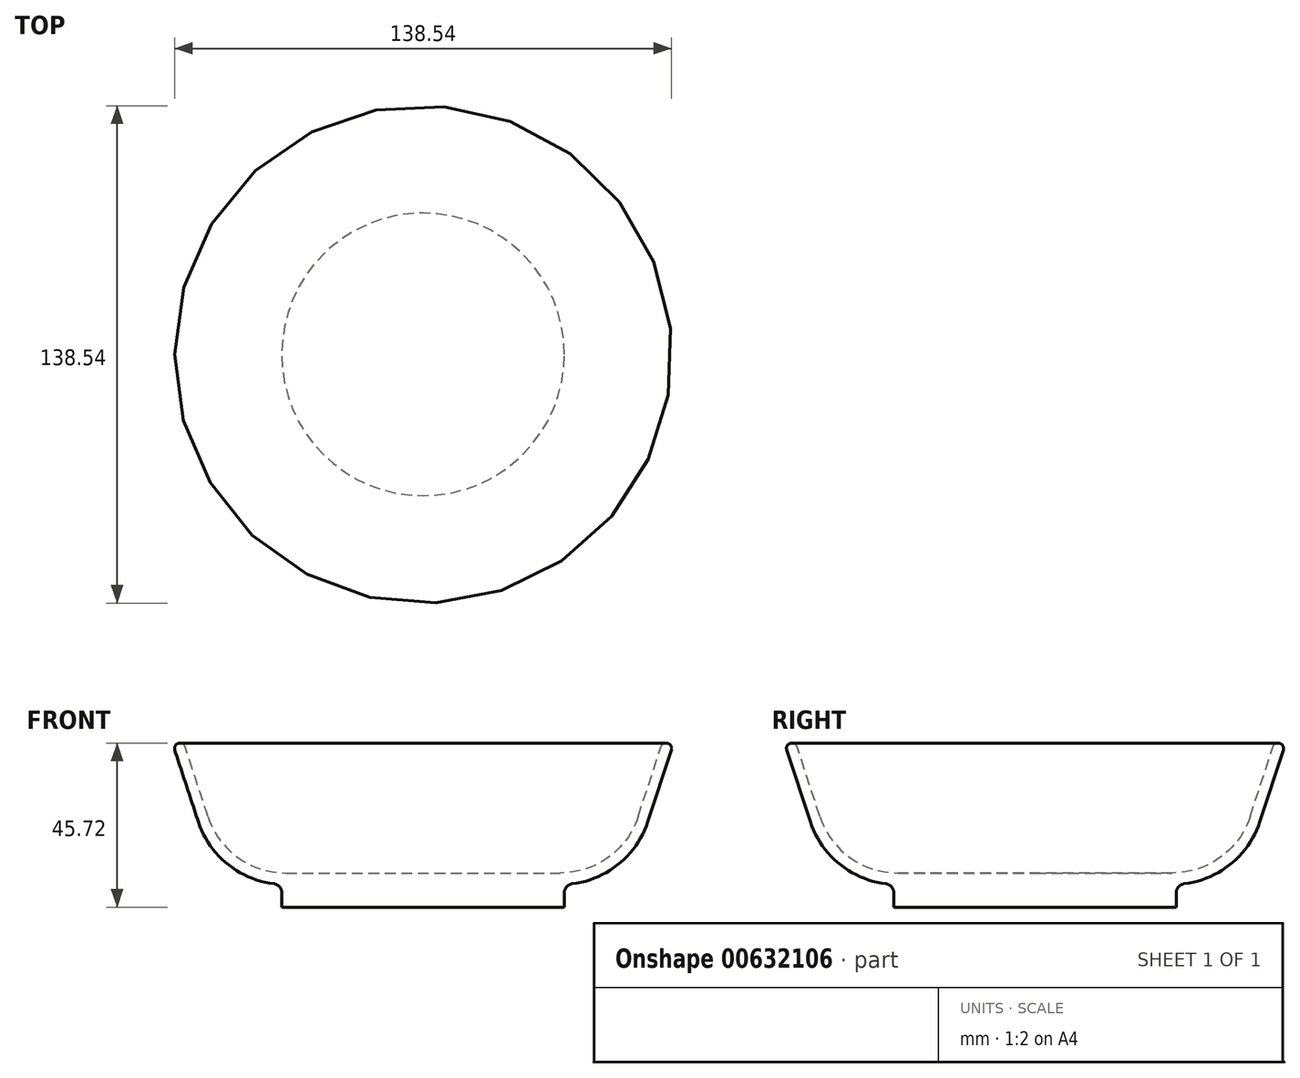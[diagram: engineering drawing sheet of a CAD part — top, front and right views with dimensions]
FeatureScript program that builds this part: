
annotation { "Feature Type Name" : "Feature", "Feature Type Description" : "" }
export const myFeature = defineFeature(function(context is Context, id is Id, definition is map)
    precondition{}
    {
        {
            var Q0;
            Q0=qCreatedBy(makeId("Front.planeOp"),FACE);
            var sketch = newSketch(context, id + "F0", { "sketchPlane" : qUnion([Q0])});
            skLineSegment(sketch, "E0.bottom", {"start": v(-76.2, 0) * mm, "end": v(63.5, 0) * mm, "construction": true});
            skLineSegment(sketch, "E0.top", {"start": v(62.55, 45.72) * mm, "end": v(63.5, 45.72) * mm, "construction": true});
            skLineSegment(sketch, "E0.left", {"start": v(-76.2, 0) * mm, "end": v(-76.2, 45.72) * mm, "construction": true});
            skLineSegment(sketch, "E0.right", {"start": v(63.5, 0) * mm, "end": v(63.5, 45.72) * mm, "construction": true});
            skLineSegment(sketch, "E1", {"start": v(25.4, 63.9) * mm, "end": v(25.4, -32.83) * mm, "construction": true});
            skLineSegment(sketch, "E2", {"start": v(61.42, 45.72) * mm, "end": v(61.42, 45.72) * mm});
            skLineSegment(sketch, "E3", {"start": v(24.38, 0) * mm, "end": v(31.32, 0) * mm});
            skLineSegment(sketch, "E4", {"start": v(0, 9.52) * mm, "end": v(25.4, 9.52) * mm});
            skLineSegment(sketch, "E5", {"start": v(24.38, 0) * mm, "end": v(0, 0) * mm});
            skLineSegment(sketch, "E6", {"start": v(62.85, 43.74) * mm, "end": v(56.27, 23.78) * mm});
            skArc(sketch, "E7.filletArc", {"start": v(35.25, 6.52) * mm, "mid": v(48.27, 12.1) * mm, "end": v(56.27, 23.78) * mm});
            skLineSegment(sketch, "E8", {"start": v(59.98, 44.68) * mm, "end": v(53.6, 25.25) * mm});
            skLineSegment(sketch, "E9", {"start": v(25.4, 9.52) * mm, "end": v(31.88, 9.52) * mm});
            skArc(sketch, "E10.filletArc", {"start": v(31.88, 9.52) * mm, "mid": v(45.29, 13.87) * mm, "end": v(53.6, 25.25) * mm});
            skLineSegment(sketch, "E11", {"start": v(33.02, 4) * mm, "end": v(33.02, 0) * mm});
            skPoint(sketch, "E12.visualSharp", {"position": v(33.02, 6.34) * mm});
            skArc(sketch, "E12.filletArc", {"start": v(35.25, 6.52) * mm, "mid": v(33.66, 5.68) * mm, "end": v(33.02, 4) * mm});
            skLineSegment(sketch, "E13", {"start": v(0, 0) * mm, "end": v(33.02, 0) * mm});
            skPoint(sketch, "E14.visualSharp", {"position": v(60.33, 45.72) * mm});
            skArc(sketch, "E14.filletArc", {"start": v(61.42, 45.72) * mm, "mid": v(60.53, 45.43) * mm, "end": v(59.98, 44.68) * mm});
            skPoint(sketch, "E15.visualSharp", {"position": v(63.5, 45.72) * mm});
            skArc(sketch, "E15.filletArc", {"start": v(62.85, 43.74) * mm, "mid": v(62.64, 45.1) * mm, "end": v(61.42, 45.72) * mm});
            skLineSegment(sketch, "E16.0", {"start": v(-6.35, 0) * mm, "end": v(-6.35, 9.52) * mm});
            skLineSegment(sketch, "E17", {"start": v(-6.35, 9.52) * mm, "end": v(0, 9.52) * mm});
            skLineSegment(sketch, "E18", {"start": v(-6.35, 0) * mm, "end": v(0, 0) * mm});
            skSolve(sketch);
        }
        {
            var Q0;
            Q0=makeQuery(id+"F0.imprint","IMPRINT",FACE,{"disambiguationData":[TD([[makeQuery(id+"F0.imprint","IMPRINT",EDGE,{"derivedFrom":sQuery(id+"F0.wireOp",EDGE,"E2")}),1.0]])]});
            var Q1;
            Q1=sQuery(id+"F0.wireOp",EDGE,"E16.0");
            revolve(context, id + "F1", {"surfaceOperationType" : NewSurfaceOperationType.NEW, "entities" : qUnion([Q0]), "axis" : qUnion([Q1]), "revolveType" : RevolveType.FULL});
        }
    });
